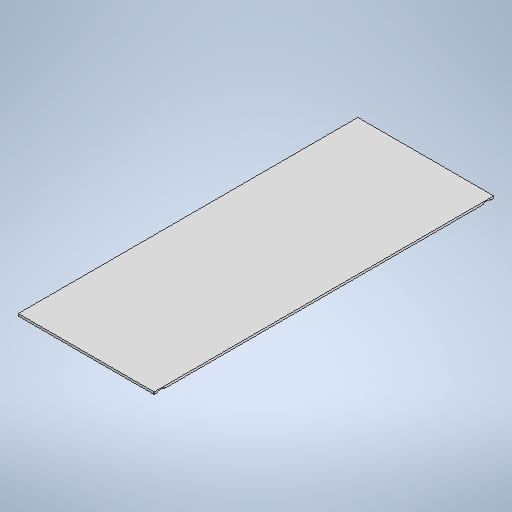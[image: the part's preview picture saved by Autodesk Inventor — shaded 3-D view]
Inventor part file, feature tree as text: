
AUTODESK INVENTOR PART (.ipt)
format: ipt  version: 2025.2 (Build 292293000, 293)  size: 268,288 bytes
history: native  units: mm
features: extrude x2, sketch x2, other x1, mirror x1
ambient origin geometry x8: Origin, YZ Plane, XZ Plane, XY Plane, X Axis, Y Axis, Z Axis, Center Point
bodies: Body1 (feature_tree)
feature tree (6):
  other  "Sólido1"
  extrude  "Extrusão1"  Depth=1500.0mm
  extrude  "Extrusão3"  Depth=10.0mm TaperAngle=0.0deg
  mirror  "Espelhar1"
  sketch  "Esboço1"  dims[d0=600.0mm d1=1500.0mm]
  sketch  "Esboço3"  dims[d2=2.0mm d3=10.0mm d4=0.0mm d13=30.5mm d14=600.0mm d15=705.0mm d16=14.5mm d20=5.0mm d21=0.0mm d10=0.5mm d11=0.872665mm d12=0.5mm d22=0.5mm d23=0.872665mm]
